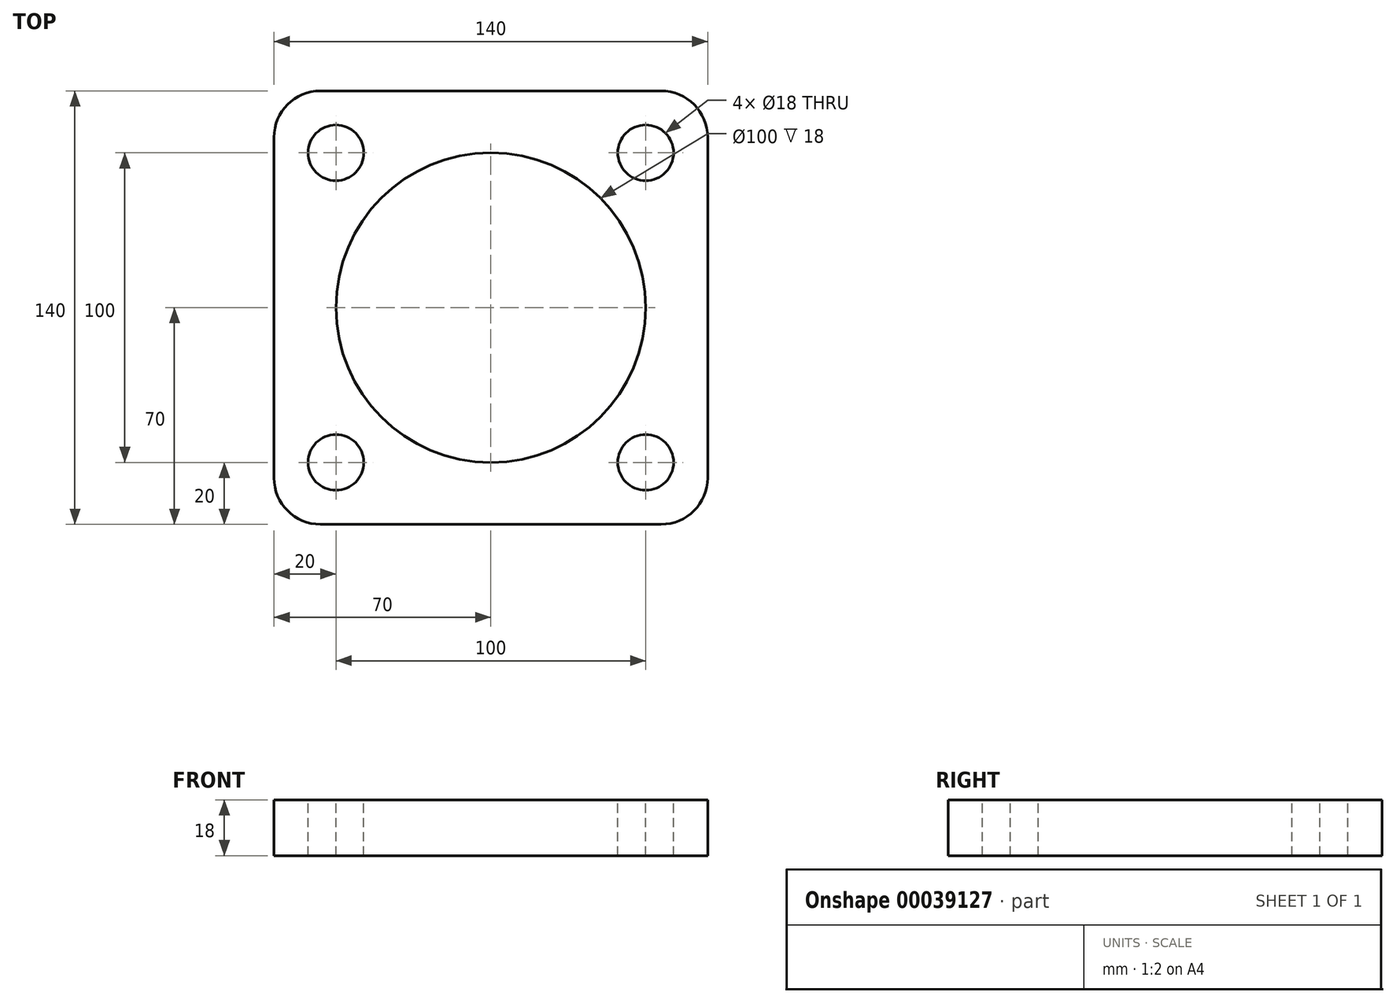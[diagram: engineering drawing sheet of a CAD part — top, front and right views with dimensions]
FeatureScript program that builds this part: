
annotation { "Feature Type Name" : "Feature", "Feature Type Description" : "" }
export const myFeature = defineFeature(function(context is Context, id is Id, definition is map)
    precondition{}
    {
        {
            var Q0;
            Q0=qCreatedBy(makeId("Top.planeOp"),FACE);
            var sketch = newSketch(context, id + "F0", { "sketchPlane" : qUnion([Q0])});
            skLineSegment(sketch, "E0", {"start": v(0, -140) * mm, "end": v(140, -140) * mm});
            skLineSegment(sketch, "E1", {"start": v(140, -140) * mm, "end": v(140, 0) * mm});
            skLineSegment(sketch, "E2", {"start": v(140, 0) * mm, "end": v(0, 0) * mm});
            skLineSegment(sketch, "E3", {"start": v(0, 0) * mm, "end": v(0, -140) * mm});
            skSolve(sketch);
        }
        {
            var Q0;
            Q0 = qSketchRegion(id + "F0", true);
            extrude(context, id + "F1", {"entities" : qUnion([Q0]), "depth" : 18 * mm});
        }
        {
            var Q0;
            Q0=makeQuery(id+"F1.opExtrude","SWEPT_EDGE",EDGE,{"disambiguationData":[OSD([sQuery(id+"F0.wireOp",EDGE,"E0"),sQuery(id+"F0.wireOp",EDGE,"E3")])]});
            var Q1;
            Q1=makeQuery(id+"F1.opExtrude","SWEPT_EDGE",EDGE,{"disambiguationData":[OSD([sQuery(id+"F0.wireOp",EDGE,"E0"),sQuery(id+"F0.wireOp",EDGE,"E1")])]});
            var Q2;
            Q2=makeQuery(id+"F1.opExtrude","SWEPT_EDGE",EDGE,{"disambiguationData":[OSD([sQuery(id+"F0.wireOp",EDGE,"E1"),sQuery(id+"F0.wireOp",EDGE,"E2")])]});
            var Q3;
            Q3=makeQuery(id+"F1.opExtrude","SWEPT_EDGE",EDGE,{"disambiguationData":[OSD([sQuery(id+"F0.wireOp",EDGE,"E2"),sQuery(id+"F0.wireOp",EDGE,"E3")])]});
            fillet(context, id + "F2", {"entities" : qUnion([Q0, Q1, Q2, Q3]), "radius" : 15 * mm, "tangentPropagation" : true, "allowEdgeOverflow" : false});
        }
        {
            var Q0;
            Q0=makeQuery(id+"F1.opExtrude","CAP_FACE",FACE,{"disambiguationData":[OSD([sQuery(id+"F0.wireOp",EDGE,"E0"),sQuery(id+"F0.wireOp",EDGE,"E1"),sQuery(id+"F0.wireOp",EDGE,"E2"),sQuery(id+"F0.wireOp",EDGE,"E3")])],"isStart":false});
            var sketch = newSketch(context, id + "F3", { "sketchPlane" : qUnion([Q0])});
            skPoint(sketch, "E4", {"position": v(120, -120) * mm});
            skPoint(sketch, "E5", {"position": v(20, -120) * mm});
            skPoint(sketch, "E6", {"position": v(20, -20) * mm});
            skPoint(sketch, "E7", {"position": v(120, -20) * mm});
            skSolve(sketch);
        }
        {
            var Q0;
            Q0=sQuery(id+"F3.wireOp",VERTEX,"E4");
            var Q1;
            Q1=sQuery(id+"F3.wireOp",VERTEX,"E5");
            var Q2;
            Q2=sQuery(id+"F3.wireOp",VERTEX,"E6");
            var Q3;
            Q3=sQuery(id+"F3.wireOp",VERTEX,"E7");
            var Q4;
            Q4=makeQuery(id+"F1.opExtrude","SWEPT_BODY",BODY,{"disambiguationData":[OSD([sQuery(id+"F0.wireOp",EDGE,"E0"),sQuery(id+"F0.wireOp",EDGE,"E1"),sQuery(id+"F0.wireOp",EDGE,"E2"),sQuery(id+"F0.wireOp",EDGE,"E3")])]});
            hole(context, id + "F4", {"style" : HoleStyle.SIMPLE, "holeDiameter" : 18 * mm, "endStyle" : HoleEndStyle.THROUGH, "locations" : qUnion([Q0, Q1, Q2, Q3]), "scope" : qUnion([Q4])});
        }
        {
            var Q0;
            Q0=makeQuery(id+"F1.opExtrude","CAP_FACE",FACE,{"disambiguationData":[OSD([sQuery(id+"F0.wireOp",EDGE,"E0"),sQuery(id+"F0.wireOp",EDGE,"E1"),sQuery(id+"F0.wireOp",EDGE,"E2"),sQuery(id+"F0.wireOp",EDGE,"E3")])],"isStart":false});
            var sketch = newSketch(context, id + "F5", { "sketchPlane" : qUnion([Q0])});
            skCircle(sketch, "E8", {"center": v(70, -70) * mm, "radius": 50 * mm});
            skSolve(sketch);
        }
        {
            var Q0;
            Q0 = qSketchRegion(id + "F5", true);
            extrude(context, id + "F6", {"entities" : qUnion([Q0]), "operationType" : NewBodyOperationType.REMOVE, "endBound" : BoundingType.THROUGH_ALL, "oppositeDirection" : true, "depth" : 25 * mm});
        }
    });
